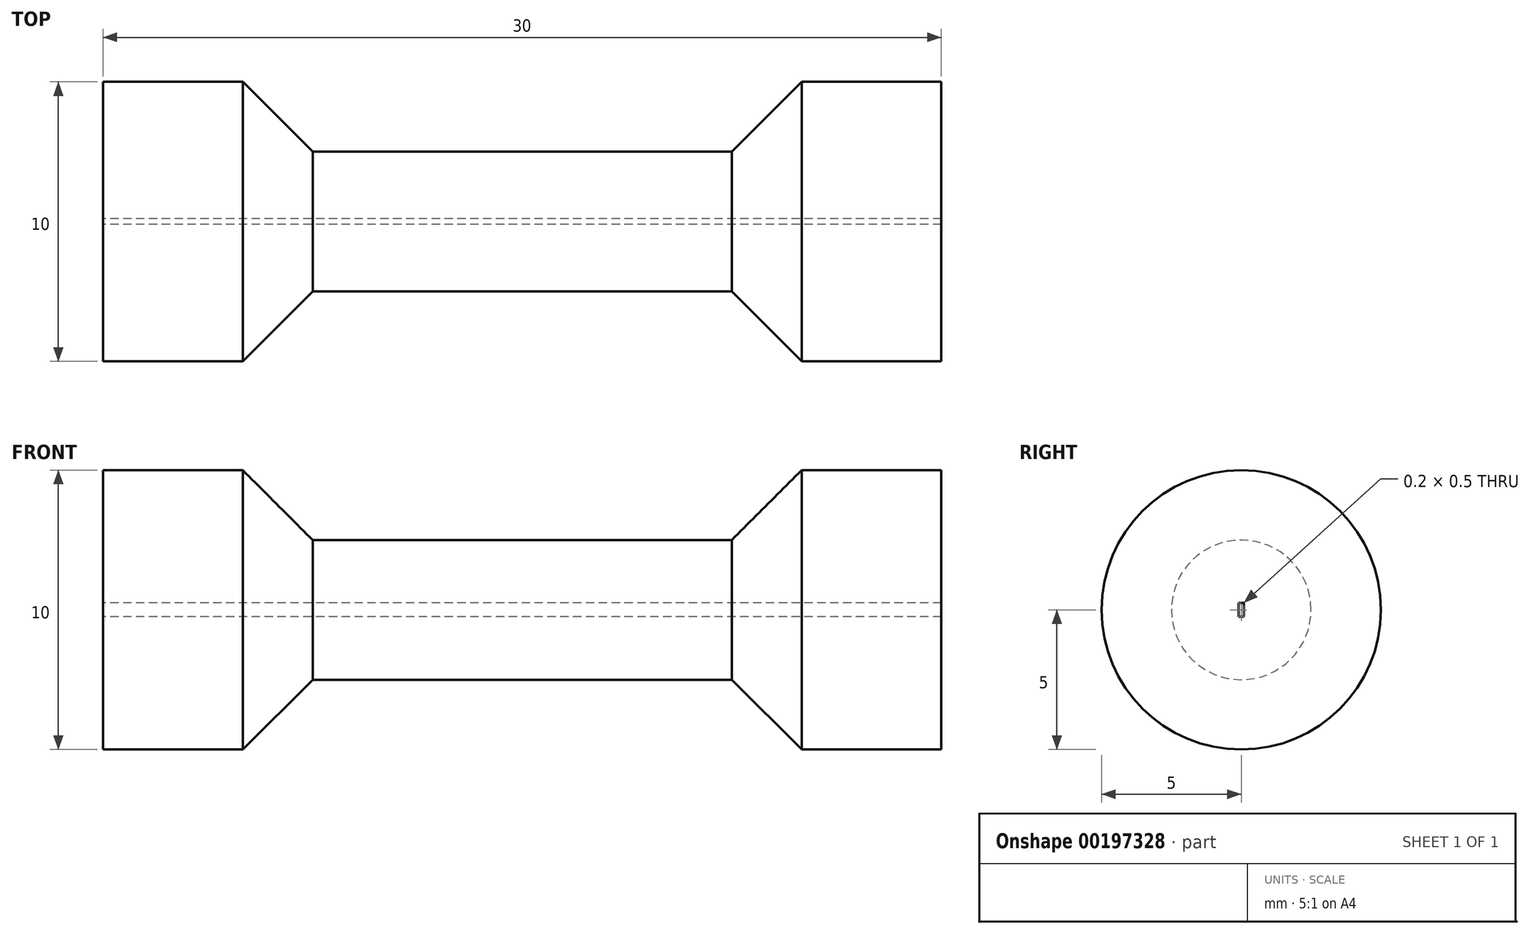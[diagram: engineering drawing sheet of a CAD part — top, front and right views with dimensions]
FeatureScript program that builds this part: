
annotation { "Feature Type Name" : "Feature", "Feature Type Description" : "" }
export const myFeature = defineFeature(function(context is Context, id is Id, definition is map)
    precondition{}
    {
        {
            var Q0;
            Q0=qCreatedBy(makeId("Front.planeOp"),FACE);
            var sketch = newSketch(context, id + "F0", { "sketchPlane" : qUnion([Q0])});
            skLineSegment(sketch, "E0", {"start": v(0, 0) * mm, "end": v(0, 5) * mm});
            skLineSegment(sketch, "E1", {"start": v(0, 5) * mm, "end": v(5, 5) * mm});
            skLineSegment(sketch, "E2", {"start": v(5, 5) * mm, "end": v(7.5, 2.5) * mm});
            skLineSegment(sketch, "E3", {"start": v(7.5, 2.5) * mm, "end": v(22.5, 2.5) * mm});
            skLineSegment(sketch, "E4", {"start": v(22.5, 2.5) * mm, "end": v(25, 5) * mm});
            skLineSegment(sketch, "E5", {"start": v(25, 5) * mm, "end": v(30, 5) * mm});
            skLineSegment(sketch, "E6", {"start": v(30, 5) * mm, "end": v(30, 0) * mm});
            skLineSegment(sketch, "E7", {"start": v(0, 0) * mm, "end": v(30, 0) * mm});
            skSolve(sketch);
        }
        {
            var Q0;
            Q0=makeQuery(id+"F0.imprint","IMPRINT",FACE,{"disambiguationData":[TD([[makeQuery(id+"F0.imprint","IMPRINT",EDGE,{"derivedFrom":sQuery(id+"F0.wireOp",EDGE,"E0")}),-1.0]])]});
            var Q1;
            Q1=sQuery(id+"F0.wireOp",EDGE,"E7");
            revolve(context, id + "F1", {"entities" : qUnion([Q0]), "axis" : qUnion([Q1]), "revolveType" : RevolveType.FULL});
        }
        {
            var Q0;
            Q0=qCreatedBy(makeId("Front.planeOp"),FACE);
            var sketch = newSketch(context, id + "F2", { "sketchPlane" : qUnion([Q0])});
            skLineSegment(sketch, "E8.0", {"start": v(30, -5) * mm, "end": v(30, 5) * mm});
            skLineSegment(sketch, "E9.0", {"start": v(0, -5) * mm, "end": v(0, 5) * mm});
            skLineSegment(sketch, "E10", {"start": v(0, 0) * mm, "end": v(30, 0) * mm});
            skSolve(sketch);
        }
        {
            var Q0;
            Q0=makeQuery(id+"F1.opRevolve","SWEPT_FACE",FACE,{"disambiguationData":[OSD([sQuery(id+"F0.wireOp",EDGE,"E6")])]});
            var sketch = newSketch(context, id + "F3", { "sketchPlane" : qUnion([Q0])});
            skPoint(sketch, "E11.0", {"position": v(0, 0) * mm});
            skLineSegment(sketch, "E12.bottom", {"start": v(0.1, -0.25) * mm, "end": v(-0.1, -0.25) * mm});
            skLineSegment(sketch, "E12.top", {"start": v(0.1, 0.25) * mm, "end": v(-0.1, 0.25) * mm});
            skLineSegment(sketch, "E12.left", {"start": v(0.1, -0.25) * mm, "end": v(0.1, 0.25) * mm});
            skLineSegment(sketch, "E12.right", {"start": v(-0.1, -0.25) * mm, "end": v(-0.1, 0.25) * mm});
            skSolve(sketch);
        }
        {
            var Q0;
            Q0 = qSketchRegion(id + "F3", true);
            var Q1;
            Q1=sQuery(id+"F2.wireOp",EDGE,"E10");
            sweep(context, id + "F4", {"profiles" : qUnion([Q0]), "path" : qUnion([Q1])});
        }
        {
            var Q0;
            Q0 = qSketchRegion(id + "F3", true);
            var Q1;
            Q1 = qConstructionFilter(qBodyType(qCreatedBy(id + "F3" ,EDGE), BodyType.WIRE), ConstructionObject.NO);
            var Q2;
            Q2=sQuery(id+"F2.wireOp",EDGE,"E10");
            var Q3;
            Q3=sQuery(id+"F2.wireOp",EDGE,"E10");
            sweep(context, id + "F5", {"operationType" : NewBodyOperationType.REMOVE, "profiles" : qUnion([Q0]), "surfaceProfiles" : qUnion([Q1, Q2]), "path" : qUnion([Q3])});
        }
    });
